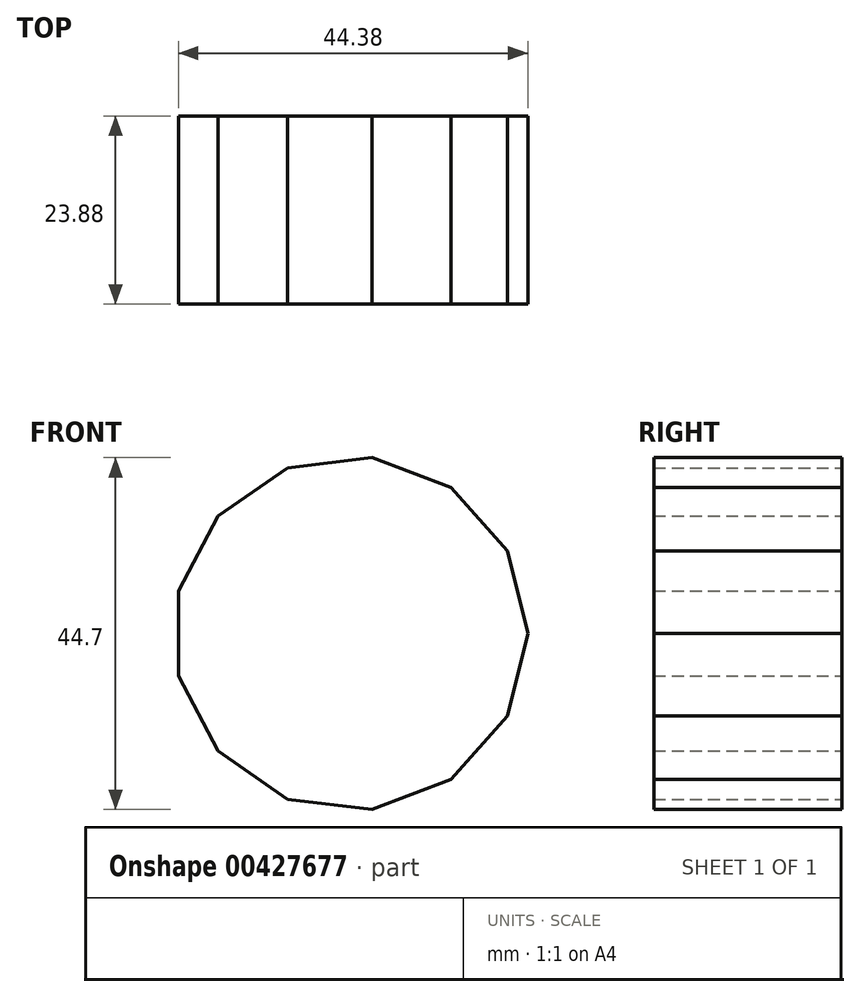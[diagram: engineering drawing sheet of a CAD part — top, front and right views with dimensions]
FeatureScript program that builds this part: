
annotation { "Feature Type Name" : "Feature", "Feature Type Description" : "" }
export const myFeature = defineFeature(function(context is Context, id is Id, definition is map)
    precondition{}
    {
        {
            var Q0;
            Q0=qCreatedBy(makeId("Front.planeOp"),FACE);
            var sketch = newSketch(context, id + "F0", { "sketchPlane" : qUnion([Q0])});
            skCircle(sketch, "E0.cCircle", {"center": v(0, 0) * mm, "radius": 21.86 * mm, "construction": true});
            skLineSegment(sketch, "E0.0", {"start": v(-21.86, -5.39) * mm, "end": v(-21.86, 5.39) * mm});
            skLineSegment(sketch, "E0.1", {"start": v(-21.86, 5.39) * mm, "end": v(-16.85, 14.93) * mm});
            skLineSegment(sketch, "E0.2", {"start": v(-16.85, 14.93) * mm, "end": v(-7.98, 21.05) * mm});
            skLineSegment(sketch, "E0.3", {"start": v(-7.98, 21.05) * mm, "end": v(2.71, 22.35) * mm});
            skLineSegment(sketch, "E0.4", {"start": v(2.71, 22.35) * mm, "end": v(12.8, 18.53) * mm});
            skLineSegment(sketch, "E0.5", {"start": v(12.8, 18.53) * mm, "end": v(19.94, 10.46) * mm});
            skLineSegment(sketch, "E0.6", {"start": v(19.94, 10.46) * mm, "end": v(22.52, 0) * mm});
            skLineSegment(sketch, "E0.7", {"start": v(22.52, 0) * mm, "end": v(19.94, -10.46) * mm});
            skLineSegment(sketch, "E0.8", {"start": v(19.94, -10.46) * mm, "end": v(12.8, -18.53) * mm});
            skLineSegment(sketch, "E0.9", {"start": v(12.8, -18.53) * mm, "end": v(2.71, -22.35) * mm});
            skLineSegment(sketch, "E0.10", {"start": v(2.71, -22.35) * mm, "end": v(-7.98, -21.05) * mm});
            skLineSegment(sketch, "E0.11", {"start": v(-7.98, -21.05) * mm, "end": v(-16.85, -14.93) * mm});
            skLineSegment(sketch, "E0.12", {"start": v(-16.85, -14.93) * mm, "end": v(-21.86, -5.39) * mm});
            skPoint(sketch, "E0.0.midPoint", {"position": v(-21.86, 0) * mm});
            skSolve(sketch);
        }
        {
            var Q0;
            Q0=makeQuery(id+"F0.imprint","IMPRINT",FACE,{"disambiguationData":[TD([[makeQuery(id+"F0.imprint","IMPRINT",EDGE,{"derivedFrom":sQuery(id+"F0.wireOp",EDGE,"E0.0")}),-1.0]])]});
            extrude(context, id + "F1", {"entities" : qUnion([Q0]), "depth" : 23.88 * mm});
        }
    });
